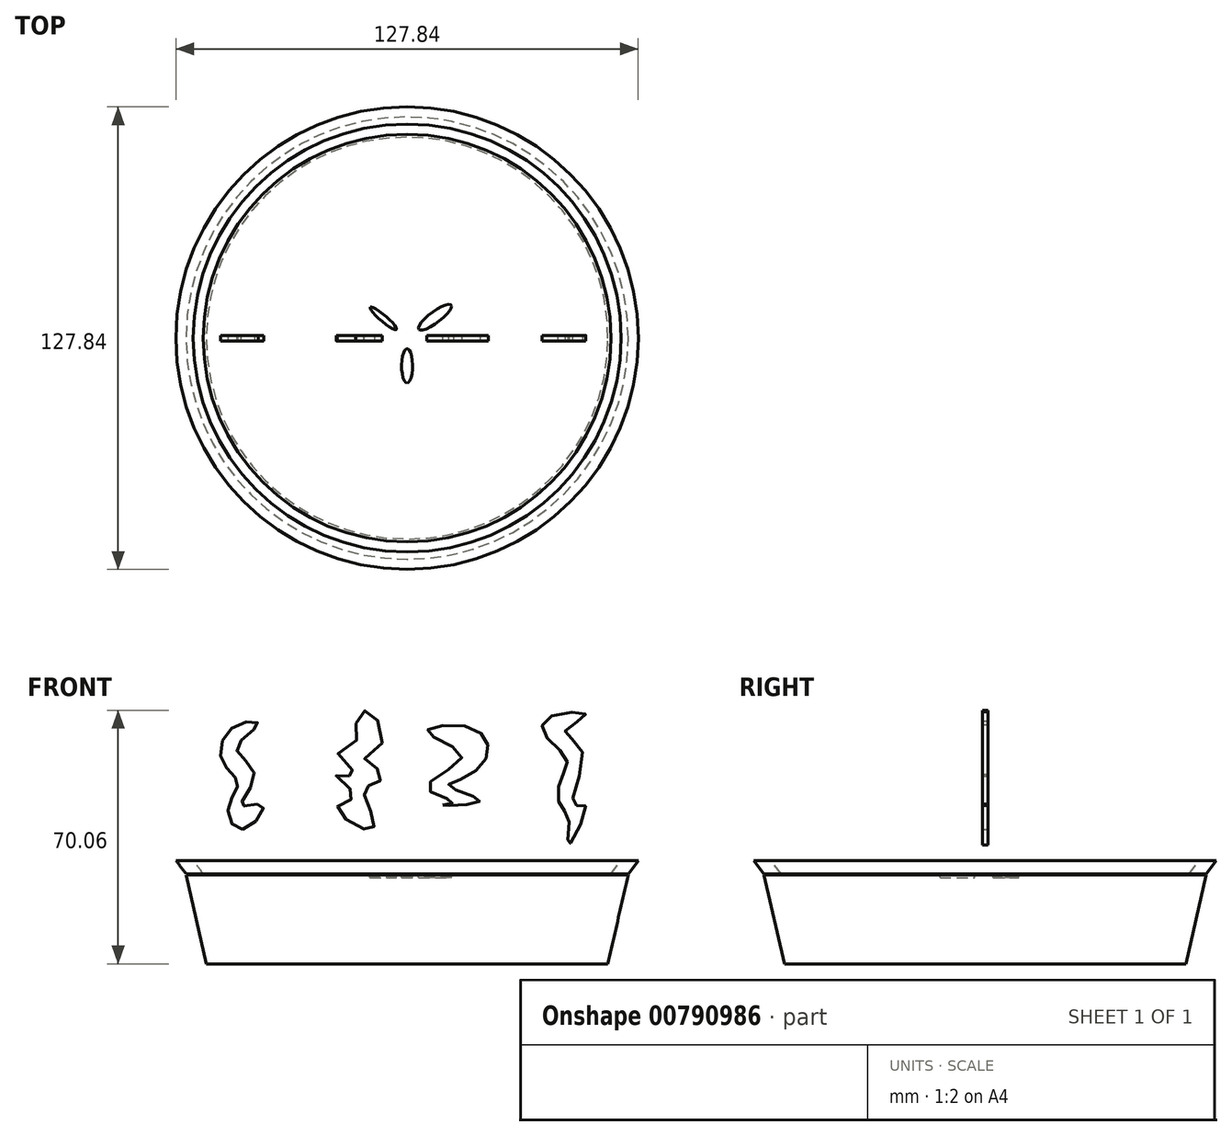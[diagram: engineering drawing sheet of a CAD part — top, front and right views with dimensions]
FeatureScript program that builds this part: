
annotation { "Feature Type Name" : "Feature", "Feature Type Description" : "" }
export const myFeature = defineFeature(function(context is Context, id is Id, definition is map)
    precondition{}
    {
        {
            var Q0;
            Q0=qCreatedBy(makeId("Front.planeOp"),FACE);
            var sketch = newSketch(context, id + "F0", { "sketchPlane" : qUnion([Q0])});
            skLineSegment(sketch, "E0", {"start": v(-61.13, 37.35) * mm, "end": v(0, 37.35) * mm});
            skLineSegment(sketch, "E1", {"start": v(0, 37.35) * mm, "end": v(0, 12.73) * mm});
            skLineSegment(sketch, "E2", {"start": v(0, 12.73) * mm, "end": v(-55.53, 12.73) * mm});
            skLineSegment(sketch, "E3", {"start": v(-55.53, 12.73) * mm, "end": v(-61.13, 37.35) * mm});
            skSolve(sketch);
        }
        {
            var Q0;
            Q0=makeQuery(id+"F0.imprint","IMPRINT",FACE,{"disambiguationData":[TD([[makeQuery(id+"F0.imprint","IMPRINT",EDGE,{"derivedFrom":sQuery(id+"F0.wireOp",EDGE,"E0")}),-1.0]])]});
            var Q1;
            Q1=sQuery(id+"F0.wireOp",EDGE,"E1");
            revolve(context, id + "F1", {"surfaceOperationType" : NewSurfaceOperationType.NEW, "entities" : qUnion([Q0]), "axis" : qUnion([Q1]), "revolveType" : RevolveType.FULL});
        }
        {
            var Q0;
            Q0=makeQuery(id+"F1.opRevolve","SWEPT_FACE",FACE,{"disambiguationData":[OSD([sQuery(id+"F0.wireOp",EDGE,"E0")])]});
            var sketch = newSketch(context, id + "F2", { "sketchPlane" : qUnion([Q0])});
            skPoint(sketch, "E4", {"position": v(0, 0) * mm});
            skSolve(sketch);
        }
        {
            var Q0;
            Q0=qCreatedBy(makeId("Front.planeOp"),FACE);
            var sketch = newSketch(context, id + "F3", { "sketchPlane" : qUnion([Q0])});
            skLineSegment(sketch, "E5", {"start": v(-61.13, 37.63) * mm, "end": v(-63.92, 41.26) * mm});
            skLineSegment(sketch, "E6", {"start": v(-63.92, 41.26) * mm, "end": v(-59.17, 41.26) * mm});
            skLineSegment(sketch, "E7", {"start": v(-59.17, 41.26) * mm, "end": v(-56.37, 37.63) * mm});
            skLineSegment(sketch, "E8", {"start": v(-56.37, 37.63) * mm, "end": v(-61.13, 37.63) * mm});
            skSolve(sketch);
        }
        {
            var Q0;
            Q0=makeQuery(id+"F3.imprint","IMPRINT",FACE,{"disambiguationData":[TD([[makeQuery(id+"F3.imprint","IMPRINT",EDGE,{"derivedFrom":sQuery(id+"F3.wireOp",EDGE,"E5")}),-1.0]])]});
            var Q1;
            Q1=makeQuery(id+"F1.opRevolve","SWEPT_EDGE",EDGE,{"disambiguationData":[OSD([sQuery(id+"F0.wireOp",EDGE,"E0"),sQuery(id+"F0.wireOp",EDGE,"E3")])]});
            revolve(context, id + "F4", {"surfaceOperationType" : NewSurfaceOperationType.NEW, "entities" : qUnion([Q0]), "axis" : qUnion([Q1]), "revolveType" : RevolveType.FULL});
        }
        {
            var Q0;
            Q0=makeQuery(id+"F2.imprint","IMPRINT",FACE,{"disambiguationData":[TD([[makeQuery(id+"F2.imprint","IMPRINT",EDGE,{"derivedFrom":makeQuery(id+"F1.opRevolve","SWEPT_EDGE",EDGE,{"disambiguationData":[OSD([sQuery(id+"F0.wireOp",EDGE,"E0"),sQuery(id+"F0.wireOp",EDGE,"E3")])]})}),1.0]])]});
            var sketch = newSketch(context, id + "F5", { "sketchPlane" : qUnion([Q0])});
            skEllipse(sketch, "E9", {"center": v(-6.57, 5.46) * mm, "majorRadius": 4.76 * mm, "minorRadius": 0.87 * mm, "majorAxis": v(-0.76, 0.65)});
            skEllipse(sketch, "E10", {"center": v(7.7, 5.73) * mm, "majorRadius": 5.6 * mm, "minorRadius": 1.55 * mm, "majorAxis": v(-0.8, -0.6)});
            skEllipse(sketch, "E11", {"center": v(0, -7.7) * mm, "majorRadius": 4.76 * mm, "minorRadius": 1.52 * mm, "majorAxis": v(0, -1)});
            skSolve(sketch);
        }
        {
            var Q0;
            Q0=makeQuery(id+"F5.imprint","IMPRINT",FACE,{"disambiguationData":[TD([[makeQuery(id+"F5.imprint","IMPRINT",EDGE,{"derivedFrom":sQuery(id+"F5.wireOp",EDGE,"E11")}),1.0]])]});
            var Q1;
            Q1=makeQuery(id+"F5.imprint","IMPRINT",FACE,{"disambiguationData":[TD([[makeQuery(id+"F5.imprint","IMPRINT",EDGE,{"derivedFrom":sQuery(id+"F5.wireOp",EDGE,"E10")}),1.0]])]});
            var Q2;
            Q2=makeQuery(id+"F5.imprint","IMPRINT",FACE,{"disambiguationData":[TD([[makeQuery(id+"F5.imprint","IMPRINT",EDGE,{"derivedFrom":sQuery(id+"F5.wireOp",EDGE,"E9")}),1.0]])]});
            extrude(context, id + "F6", {"entities" : qUnion([Q0, Q1, Q2]), "operationType" : NewBodyOperationType.REMOVE, "oppositeDirection" : true, "depth" : 0.76 * mm, "offsetDistance" : 25.4 * mm});
        }
        {
            var Q0;
            Q0=qCreatedBy(makeId("Front.planeOp"),FACE);
            var sketch = newSketch(context, id + "F7", { "sketchPlane" : qUnion([Q0])});
            skFitSpline(sketch, "E12", {"points": [v(-45.52, 49.86) * mm, v(-49.5, 55.82) * mm, v(-46.84, 62.78) * mm, v(-51.15, 68.75) * mm, v(-47.84, 78.36) * mm, v(-41.2, 79.02) * mm, v(-47.17, 72.4) * mm, v(-42.2, 65.1) * mm, v(-45.85, 56.48) * mm, v(-39.88, 56.6) * mm, v(-45.52, 49.86) * mm]});
            skFitSpline(sketch, "E13", {"points": [v(-14.17, 79.2) * mm, v(-14.7, 73.05) * mm, v(-19.32, 71.48) * mm, v(-14.36, 64.77) * mm, v(-19.6, 64.9) * mm, v(-14.46, 59.17) * mm, v(-19.04, 56.6) * mm, v(-14.74, 51.16) * mm, v(-9.3, 50.3) * mm, v(-10.72, 56.6) * mm, v(-11.6, 61.46) * mm, v(-7.59, 63.18) * mm, v(-8.4, 66.76) * mm, v(-12.05, 70.07) * mm, v(-7.4, 72.4) * mm, v(-10.45, 82.65) * mm, v(-14.17, 79.2) * mm]});
            skFitSpline(sketch, "E14", {"points": [v(9.83, 56.6) * mm, v(12.81, 57.48) * mm, v(5.52, 61.45) * mm, v(15.13, 70.07) * mm, v(5.52, 76.7) * mm, v(16.46, 78.36) * mm, v(22.42, 72.4) * mm, v(17.12, 64.77) * mm, v(11.48, 61.79) * mm, v(20.1, 58.14) * mm, v(14.47, 56.6) * mm, v(9.83, 56.6) * mm]});
            skFitSpline(sketch, "E15", {"points": [v(39.93, 81.21) * mm, v(37.64, 76.63) * mm, v(44.23, 69.2) * mm, v(42.51, 64.04) * mm, v(42.3, 56.6) * mm, v(44.8, 52.59) * mm, v(44.63, 45.55) * mm, v(49.27, 56.6) * mm, v(45.95, 56.6) * mm, v(48.24, 72.05) * mm, v(43.66, 76.92) * mm, v(49.38, 81.5) * mm, v(39.93, 81.21) * mm]});
            skSolve(sketch);
        }
        {
            var Q0;
            Q0=makeQuery(id+"F7.imprint","IMPRINT",FACE,{"disambiguationData":[TD([[makeQuery(id+"F7.imprint","IMPRINT",EDGE,{"derivedFrom":sQuery(id+"F7.wireOp",EDGE,"E12")}),-1.0]])]});
            var Q1;
            Q1=makeQuery(id+"F7.imprint","IMPRINT",FACE,{"disambiguationData":[TD([[makeQuery(id+"F7.imprint","IMPRINT",EDGE,{"derivedFrom":sQuery(id+"F7.wireOp",EDGE,"E13")}),1.0]])]});
            var Q2;
            Q2=makeQuery(id+"F7.imprint","IMPRINT",FACE,{"disambiguationData":[TD([[makeQuery(id+"F7.imprint","IMPRINT",EDGE,{"derivedFrom":sQuery(id+"F7.wireOp",EDGE,"E14")}),-1.0]])]});
            var Q3;
            Q3=makeQuery(id+"F7.imprint","IMPRINT",FACE,{"disambiguationData":[TD([[makeQuery(id+"F7.imprint","IMPRINT",EDGE,{"derivedFrom":sQuery(id+"F7.wireOp",EDGE,"E15")}),1.0]])]});
            extrude(context, id + "F8", {"entities" : qUnion([Q0, Q1, Q2, Q3]), "endBound" : BoundingType.SYMMETRIC, "oppositeDirection" : true, "depth" : 1.52 * mm, "offsetDistance" : 25.4 * mm});
        }
    });
